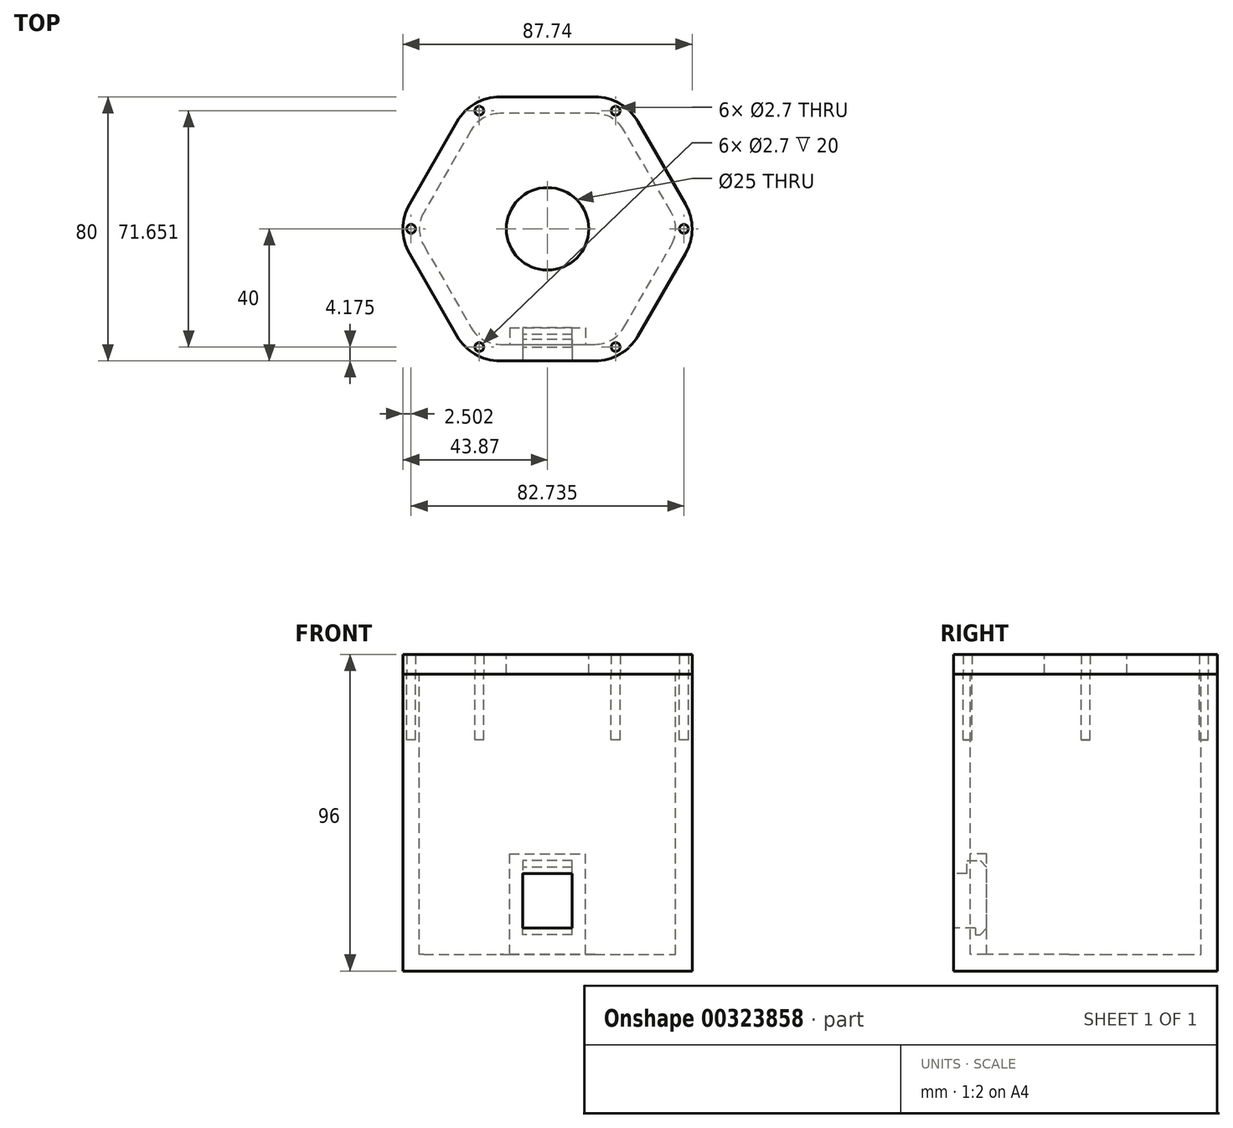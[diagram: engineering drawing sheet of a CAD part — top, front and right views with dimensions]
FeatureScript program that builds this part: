
annotation { "Feature Type Name" : "Feature", "Feature Type Description" : "" }
export const myFeature = defineFeature(function(context is Context, id is Id, definition is map)
    precondition{}
    {
        {
            assignVariable(context, id + "F0", {"name" : "Height", "anyValue" : 90});
        }
        {
            assignVariable(context, id + "F1", {"name" : "WallThickness", "anyValue" : 5});
        }
        {
            assignVariable(context, id + "F2", {"name" : "TopThickness", "anyValue" : 6});
        }
        {
            assignVariable(context, id + "F3", {"name" : "CornerRounding", "anyValue" : 15});
        }
        {
            assignVariable(context, id + "F4", {"name" : "ScrewDepth", "anyValue" : 20});
        }
        {
            var Q0;
            Q0=qCreatedBy(makeId("Top.planeOp"),FACE);
            var sketch = newSketch(context, id + "F5", { "sketchPlane" : qUnion([Q0])});
            skCircle(sketch, "E0.cCircle", {"center": v(0, 0) * mm, "radius": 40 * mm, "construction": true});
            skLineSegment(sketch, "E0.0", {"start": v(-23.1, 40) * mm, "end": v(23.1, 40) * mm});
            skLineSegment(sketch, "E0.1", {"start": v(23.1, 40) * mm, "end": v(46.19, 0) * mm});
            skLineSegment(sketch, "E0.2", {"start": v(46.19, 0) * mm, "end": v(23.1, -40) * mm});
            skLineSegment(sketch, "E0.3", {"start": v(23.1, -40) * mm, "end": v(-23.1, -40) * mm});
            skLineSegment(sketch, "E0.4", {"start": v(-23.1, -40) * mm, "end": v(-46.19, 0) * mm});
            skLineSegment(sketch, "E0.5", {"start": v(-46.19, 0) * mm, "end": v(-23.1, 40) * mm});
            skPoint(sketch, "E0.0.midPoint", {"position": v(0, 40) * mm});
            skSolve(sketch);
        }
        {
            var Q0;
            Q0=makeQuery(id+"F5.imprint","IMPRINT",FACE,{"disambiguationData":[TD([[makeQuery(id+"F5.imprint","IMPRINT",EDGE,{"derivedFrom":sQuery(id+"F5.wireOp",EDGE,"E0.0")}),-1.0]])]});
            extrude(context, id + "F6", {"entities" : qUnion([Q0]), "depth" : (getVariable(context, 'Height')) * mm});
        }
        {
            var Q0;
            Q0=makeQuery(id+"F6.opExtrude","SWEPT_EDGE",EDGE,{"disambiguationData":[OSD([sQuery(id+"F5.wireOp",EDGE,"E0.3"),sQuery(id+"F5.wireOp",EDGE,"E0.4")])]});
            var Q1;
            Q1=makeQuery(id+"F6.opExtrude","SWEPT_EDGE",EDGE,{"disambiguationData":[OSD([sQuery(id+"F5.wireOp",EDGE,"E0.4"),sQuery(id+"F5.wireOp",EDGE,"E0.5")])]});
            var Q2;
            Q2=makeQuery(id+"F6.opExtrude","SWEPT_EDGE",EDGE,{"disambiguationData":[OSD([sQuery(id+"F5.wireOp",EDGE,"E0.0"),sQuery(id+"F5.wireOp",EDGE,"E0.5")])]});
            var Q3;
            Q3=makeQuery(id+"F6.opExtrude","SWEPT_EDGE",EDGE,{"disambiguationData":[OSD([sQuery(id+"F5.wireOp",EDGE,"E0.0"),sQuery(id+"F5.wireOp",EDGE,"E0.1")])]});
            var Q4;
            Q4=makeQuery(id+"F6.opExtrude","SWEPT_EDGE",EDGE,{"disambiguationData":[OSD([sQuery(id+"F5.wireOp",EDGE,"E0.1"),sQuery(id+"F5.wireOp",EDGE,"E0.2")])]});
            var Q5;
            Q5=makeQuery(id+"F6.opExtrude","SWEPT_EDGE",EDGE,{"disambiguationData":[OSD([sQuery(id+"F5.wireOp",EDGE,"E0.2"),sQuery(id+"F5.wireOp",EDGE,"E0.3")])]});
            fillet(context, id + "F7", {"entities" : qUnion([Q0, Q1, Q2, Q3, Q4, Q5]), "radius" : (getVariable(context, 'CornerRounding')) * mm, "tangentPropagation" : true, "allowEdgeOverflow" : false});
        }
        {
            var Q0;
            Q0=makeQuery(id+"F6.opExtrude","CAP_FACE",FACE,{"disambiguationData":[OSD([sQuery(id+"F5.wireOp",EDGE,"E0.0"),sQuery(id+"F5.wireOp",EDGE,"E0.1"),sQuery(id+"F5.wireOp",EDGE,"E0.2"),sQuery(id+"F5.wireOp",EDGE,"E0.3"),sQuery(id+"F5.wireOp",EDGE,"E0.4"),sQuery(id+"F5.wireOp",EDGE,"E0.5")])],"isStart":false});
            extrude(context, id + "F8", {"entities" : qUnion([Q0]), "depth" : (getVariable(context, 'TopThickness')) * mm});
        }
        {
            var Q0;
            Q0=makeQuery(id+"F6.opExtrude","CAP_FACE",FACE,{"disambiguationData":[OSD([sQuery(id+"F5.wireOp",EDGE,"E0.0"),sQuery(id+"F5.wireOp",EDGE,"E0.1"),sQuery(id+"F5.wireOp",EDGE,"E0.2"),sQuery(id+"F5.wireOp",EDGE,"E0.3"),sQuery(id+"F5.wireOp",EDGE,"E0.4"),sQuery(id+"F5.wireOp",EDGE,"E0.5")])],"isStart":false});
            var sketch = newSketch(context, id + "F9", { "sketchPlane" : qUnion([Q0])});
            skArc(sketch, "E1.0", {"start": v(-14.43, 35) * mm, "mid": v(-19.43, 33.66) * mm, "end": v(-23.1, 30) * mm});
            skLineSegment(sketch, "E1.1", {"start": v(-14.43, -35) * mm, "end": v(14.43, -35) * mm});
            skArc(sketch, "E1.2", {"start": v(-23.1, -30) * mm, "mid": v(-19.43, -33.66) * mm, "end": v(-14.43, -35) * mm});
            skLineSegment(sketch, "E1.3", {"start": v(-37.53, -5) * mm, "end": v(-23.1, -30) * mm});
            skArc(sketch, "E1.4", {"start": v(-37.53, 5) * mm, "mid": v(-38.87, 0) * mm, "end": v(-37.53, -5) * mm});
            skArc(sketch, "E1.5", {"start": v(14.43, -35) * mm, "mid": v(19.43, -33.66) * mm, "end": v(23.1, -30) * mm});
            skLineSegment(sketch, "E1.6", {"start": v(-23.1, 30) * mm, "end": v(-37.53, 5) * mm});
            skLineSegment(sketch, "E1.7", {"start": v(23.1, -30) * mm, "end": v(37.53, -5) * mm});
            skArc(sketch, "E1.8", {"start": v(37.53, -5) * mm, "mid": v(38.87, 0) * mm, "end": v(37.53, 5) * mm});
            skLineSegment(sketch, "E1.9", {"start": v(37.53, 5) * mm, "end": v(23.1, 30) * mm});
            skArc(sketch, "E1.10", {"start": v(23.1, 30) * mm, "mid": v(19.43, 33.66) * mm, "end": v(14.43, 35) * mm});
            skLineSegment(sketch, "E1.11", {"start": v(14.43, 35) * mm, "end": v(-14.43, 35) * mm});
            skSolve(sketch);
        }
        {
            var Q0;
            Q0=makeQuery(id+"F9.imprint","IMPRINT",FACE,{"disambiguationData":[TD([[makeQuery(id+"F9.imprint","IMPRINT",EDGE,{"derivedFrom":sQuery(id+"F9.wireOp",EDGE,"E1.0")}),1.0]])]});
            extrude(context, id + "F10", {"entities" : qUnion([Q0]), "operationType" : NewBodyOperationType.REMOVE, "oppositeDirection" : true, "depth" : (getVariable(context, 'Height') - getVariable(context, 'WallThickness')) * mm});
        }
        {
            var Q0;
            Q0=makeQuery(id+"F6.opExtrude","CAP_FACE",FACE,{"disambiguationData":[OSD([sQuery(id+"F5.wireOp",EDGE,"E0.0"),sQuery(id+"F5.wireOp",EDGE,"E0.1"),sQuery(id+"F5.wireOp",EDGE,"E0.2"),sQuery(id+"F5.wireOp",EDGE,"E0.3"),sQuery(id+"F5.wireOp",EDGE,"E0.4"),sQuery(id+"F5.wireOp",EDGE,"E0.5")])],"isStart":false});
            var sketch = newSketch(context, id + "F11", { "sketchPlane" : qUnion([Q0])});
            skLineSegment(sketch, "E2", {"start": v(-43.87, 0) * mm, "end": v(-38.87, 0) * mm, "construction": true});
            skCircle(sketch, "E3", {"center": v(-41.37, 0) * mm, "radius": 1.35 * mm});
            skCircle(sketch, "E4.1.0", {"center": v(-20.68, -35.83) * mm, "radius": 1.35 * mm});
            skCircle(sketch, "E4.2.0", {"center": v(20.68, -35.83) * mm, "radius": 1.35 * mm});
            skCircle(sketch, "E4.3.0", {"center": v(41.37, 0) * mm, "radius": 1.35 * mm});
            skCircle(sketch, "E4.4.0", {"center": v(20.68, 35.83) * mm, "radius": 1.35 * mm});
            skCircle(sketch, "E4.5.0", {"center": v(-20.68, 35.83) * mm, "radius": 1.35 * mm});
            skPoint(sketch, "E4.center", {"position": v(0, 0) * mm});
            skSolve(sketch);
        }
        {
            var Q0;
            Q0 = qSketchRegion(id + "F11", true);
            extrude(context, id + "F12", {"entities" : qUnion([Q0]), "operationType" : NewBodyOperationType.REMOVE, "oppositeDirection" : true, "depth" : (getVariable(context, 'ScrewDepth')) * mm});
        }
        {
            var Q0;
            Q0=makeQuery(id+"F11.imprint","IMPRINT",FACE,{"disambiguationData":[TD([[makeQuery(id+"F11.imprint","IMPRINT",EDGE,{"derivedFrom":sQuery(id+"F11.wireOp",EDGE,"E4.5.0")}),1.0]])]});
            var Q1;
            Q1=makeQuery(id+"F11.imprint","IMPRINT",FACE,{"disambiguationData":[TD([[makeQuery(id+"F11.imprint","IMPRINT",EDGE,{"derivedFrom":sQuery(id+"F11.wireOp",EDGE,"E3")}),1.0]])]});
            var Q2;
            Q2=makeQuery(id+"F11.imprint","IMPRINT",FACE,{"disambiguationData":[TD([[makeQuery(id+"F11.imprint","IMPRINT",EDGE,{"derivedFrom":sQuery(id+"F11.wireOp",EDGE,"E4.1.0")}),1.0]])]});
            var Q3;
            Q3=makeQuery(id+"F11.imprint","IMPRINT",FACE,{"disambiguationData":[TD([[makeQuery(id+"F11.imprint","IMPRINT",EDGE,{"derivedFrom":sQuery(id+"F11.wireOp",EDGE,"E4.3.0")}),1.0]])]});
            var Q4;
            Q4=makeQuery(id+"F11.imprint","IMPRINT",FACE,{"disambiguationData":[TD([[makeQuery(id+"F11.imprint","IMPRINT",EDGE,{"derivedFrom":sQuery(id+"F11.wireOp",EDGE,"E4.4.0")}),1.0]])]});
            var Q5;
            Q5=makeQuery(id+"F11.imprint","IMPRINT",FACE,{"disambiguationData":[TD([[makeQuery(id+"F11.imprint","IMPRINT",EDGE,{"derivedFrom":sQuery(id+"F11.wireOp",EDGE,"E4.2.0")}),1.0]])]});
            extrude(context, id + "F13", {"entities" : qUnion([Q0, Q1, Q2, Q3, Q4, Q5]), "operationType" : NewBodyOperationType.REMOVE, "oppositeDirection" : true, "depth" : -(getVariable(context, 'TopThickness')) * mm});
        }
        {
            var Q0;
            Q0=makeQuery(id+"F8.opExtrude","CAP_FACE",FACE,{"disambiguationData":[OSD([sQuery(id+"F5.wireOp",EDGE,"E0.0"),sQuery(id+"F5.wireOp",EDGE,"E0.1"),sQuery(id+"F5.wireOp",EDGE,"E0.2"),sQuery(id+"F5.wireOp",EDGE,"E0.3"),sQuery(id+"F5.wireOp",EDGE,"E0.4"),sQuery(id+"F5.wireOp",EDGE,"E0.5")])],"isStart":false});
            var sketch = newSketch(context, id + "F14", { "sketchPlane" : qUnion([Q0])});
            skCircle(sketch, "E5", {"center": v(0, 0) * mm, "radius": 12.5 * mm});
            skSolve(sketch);
        }
        {
            var Q0;
            Q0=makeQuery(id+"F14.imprint","IMPRINT",FACE,{"disambiguationData":[TD([[makeQuery(id+"F14.imprint","IMPRINT",EDGE,{"derivedFrom":sQuery(id+"F14.wireOp",EDGE,"E5")}),1.0]])]});
            extrude(context, id + "F15", {"entities" : qUnion([Q0]), "operationType" : NewBodyOperationType.REMOVE, "oppositeDirection" : true, "depth" : (getVariable(context, 'TopThickness')) * mm});
        }
        {
            var Q0;
            Q0=makeQuery(id+"F6.opExtrude","SWEPT_FACE",FACE,{"disambiguationData":[OSD([sQuery(id+"F5.wireOp",EDGE,"E0.3")])]});
            var sketch = newSketch(context, id + "F16", { "sketchPlane" : qUnion([Q0])});
            skLineSegment(sketch, "E6.bottom", {"start": v(7.5, 29.5) * mm, "end": v(-7.5, 29.5) * mm});
            skLineSegment(sketch, "E6.top", {"start": v(7.5, 13) * mm, "end": v(-7.5, 13) * mm});
            skLineSegment(sketch, "E6.left", {"start": v(7.5, 29.5) * mm, "end": v(7.5, 13) * mm});
            skLineSegment(sketch, "E6.right", {"start": v(-7.5, 29.5) * mm, "end": v(-7.5, 13) * mm});
            skPoint(sketch, "E6.middle", {"position": v(0, 21.25) * mm});
            skSolve(sketch);
        }
        {
            var Q0;
            Q0=makeQuery(id+"F16.imprint","IMPRINT",FACE,{"disambiguationData":[TD([[makeQuery(id+"F16.imprint","IMPRINT",EDGE,{"derivedFrom":sQuery(id+"F16.wireOp",EDGE,"E6.bottom")}),1.0]])]});
            extrude(context, id + "F17", {"entities" : qUnion([Q0]), "operationType" : NewBodyOperationType.REMOVE, "endBound" : BoundingType.UP_TO_NEXT, "oppositeDirection" : true, "depth" : 25 * mm});
        }
        {
            var Q0;
            Q0=makeQuery(id+"F10.boolean.opBoolean","COPY",FACE,{"derivedFrom":makeQuery(id+"F10.opExtrude","SWEPT_FACE",FACE,{"disambiguationData":[OSD([sQuery(id+"F9.wireOp",EDGE,"E1.1")])]})});
            var sketch = newSketch(context, id + "F18", { "sketchPlane" : qUnion([Q0])});
            skLineSegment(sketch, "E7.bottom", {"start": v(11.5, 5) * mm, "end": v(-11.5, 5) * mm});
            skLineSegment(sketch, "E7.top", {"start": v(11.5, 35.5) * mm, "end": v(-11.5, 35.5) * mm});
            skLineSegment(sketch, "E7.left", {"start": v(11.5, 5) * mm, "end": v(11.5, 35.5) * mm});
            skLineSegment(sketch, "E7.right", {"start": v(-11.5, 5) * mm, "end": v(-11.5, 35.5) * mm});
            skPoint(sketch, "E7.middle", {"position": v(0, 20.25) * mm});
            skSolve(sketch);
        }
        {
            var Q0;
            Q0=makeQuery(id+"F18.imprint","IMPRINT",FACE,{"disambiguationData":[TD([[makeQuery(id+"F18.imprint","IMPRINT",EDGE,{"derivedFrom":sQuery(id+"F18.wireOp",EDGE,"E7.bottom")}),-1.0]])]});
            extrude(context, id + "F19", {"entities" : qUnion([Q0]), "operationType" : NewBodyOperationType.ADD, "depth" : (10 - getVariable(context, 'WallThickness')) * mm});
        }
        {
            var Q0;
            {var subQ0=sQuery(id+"F16.wireOp",EDGE,"E6.right");Q0=makeQuery(id+"F19.boolean.opBoolean","MERGE",FACE,{"derivedFrom":[makeQuery(id+"F17.boolean.opBoolean","COPY",FACE,{"derivedFrom":makeQuery(id+"F17.opExtrude","SWEPT_FACE",FACE,{"disambiguationData":[OSD([subQ0])]})}),makeQuery(id+"F19.opExtrude","SWEPT_FACE",FACE,{"disambiguationData":[OSD([sQuery(id+"F9.wireOp",EDGE,"E1.1"),subQ0])]})]});}
            var sketch = newSketch(context, id + "F20", { "sketchPlane" : qUnion([Q0])});
            skLineSegment(sketch, "E8", {"start": v(-30, 13) * mm, "end": v(-32, 11) * mm});
            skLineSegment(sketch, "E9", {"start": v(-32, 11) * mm, "end": v(-33.5, 11) * mm});
            skLineSegment(sketch, "E10", {"start": v(-33.5, 11) * mm, "end": v(-33.5, 13) * mm});
            skLineSegment(sketch, "E11", {"start": v(-33.5, 13) * mm, "end": v(-30, 13) * mm});
            skLineSegment(sketch, "E12", {"start": v(-32, 33.5) * mm, "end": v(-36, 33.5) * mm});
            skLineSegment(sketch, "E13", {"start": v(-36, 33.5) * mm, "end": v(-36, 29.5) * mm});
            skLineSegment(sketch, "E14", {"start": v(-36, 29.5) * mm, "end": v(-30, 29.5) * mm});
            skLineSegment(sketch, "E15", {"start": v(-32, 33.5) * mm, "end": v(-30, 31.5) * mm});
            skLineSegment(sketch, "E16", {"start": v(-30, 31.5) * mm, "end": v(-30, 29.5) * mm});
            skSolve(sketch);
        }
        {
            var Q0;
            Q0 = qSketchRegion(id + "F20", true);
            var Q1;
            {var subQ0=sQuery(id+"F16.wireOp",EDGE,"E6.left");Q1=makeQuery(id+"F19.boolean.opBoolean","MERGE",FACE,{"derivedFrom":[makeQuery(id+"F17.boolean.opBoolean","COPY",FACE,{"derivedFrom":makeQuery(id+"F17.opExtrude","SWEPT_FACE",FACE,{"disambiguationData":[OSD([subQ0])]})}),makeQuery(id+"F19.opExtrude","SWEPT_FACE",FACE,{"disambiguationData":[OSD([sQuery(id+"F9.wireOp",EDGE,"E1.1"),subQ0])]})]});}
            extrude(context, id + "F21", {"entities" : qUnion([Q0]), "operationType" : NewBodyOperationType.REMOVE, "endBound" : BoundingType.UP_TO_SURFACE, "endBoundEntityFace" : qUnion([Q1]), "depth" : 25 * mm});
        }
    });
